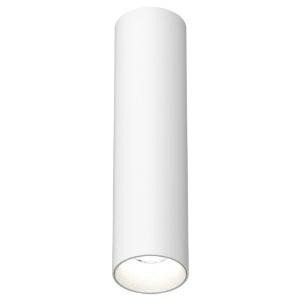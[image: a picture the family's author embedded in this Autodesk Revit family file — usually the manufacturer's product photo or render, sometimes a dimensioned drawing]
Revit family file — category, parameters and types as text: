
# Revit family: invader_o75_ab_led_10w_760lm_2700k_cri90_320-0040
name_source: partatom
category: Leuchten
revit_build: Autodesk Revit 2016 (Build: 20190508_0715(x64)
units: mm (PartAtom-declared; Revit-internal decimal feet)

## family parameters
Basisbauteil = Fläche
Beim Laden mit Abzugskörper schneiden = Nein
Bemaßung runder Anschluss = Durchmesser verwenden
Gemeinsam genutzt = Nein
Lichtquelle = Nein
Raumberechnungspunkt = Nein
Teiletyp = Normal

## types (1)
- 320-0040-K20 (1 x LED, 912.05 lm, 8.5 W, 2700K)
    Approval mark = CE
    Beschreibung = The surface luminaire INVADER ON from the familiy INVADER consists of aluminum. Stated photometric values correspond to operation by 350 mA; a suitable ballast needs to be sourced separately and is not scope of delivery. Dimming (# 320-0040) depends on the used ballast and may vary. The spot with direct illumination corresponds to protection class SK3 at IP20. A PROLICHT lense pack is optionally available.
    CIE Flux Codes = 99 100 100 100 67
    Color Rendering = 1A/90…99
    Color Temperature = 2700K
    Height = 300 mm
    Hersteller = Prolicht
    Lamp Light Flux = 912.05 lm
    Lamp Power = 8.5 W
    Lamp count = 1
    Lampe = 1 x LED
    Length = 75 mm
    Luminous efficacy = 72 lm/W
    ModVariant = Nein
    Modell = 320-0040
    Mounting Place = Ceiling
    Mounting Type = Surface mounted
    Number of Poles = 1
    OnlyDefault = Ja
    Power Factor = 1
    Product Name = INVADER Ø75 AB LED 10W 760lm 2700K CRI90
    Product group = Surface spotlights
    ProductGroupID = 332
    Protection Class = Protection class I
    Protection Degree = IP 20
    RLX_Detail_Level = 1
    RlxData = <blob elided: 25609 chars, md5=25c368e3>
    Scheinlast = 9 VA
    Socket = socket
    Standby Power = 0 W
    System Light Flux = 611 lm
    System Power = 9 W
    Typenbild = 320-0040.jpg
    URL = http://relux.com
    VarID = 320-0040-k20
    Voltage = 0 V
    Vorgabe-Ansicht = 1800 mm
    Weight = 0.00 kg
    Width = 0 mm  [stored 0 ft]

note: [stored X ft] marks values corroborated as IEEE doubles in the binary element streams (Revit-internal decimal feet)

## geometry (parser evidence)
native form markers: Blend x4, Sweep x12
no freeform markers — native parametric forms only
